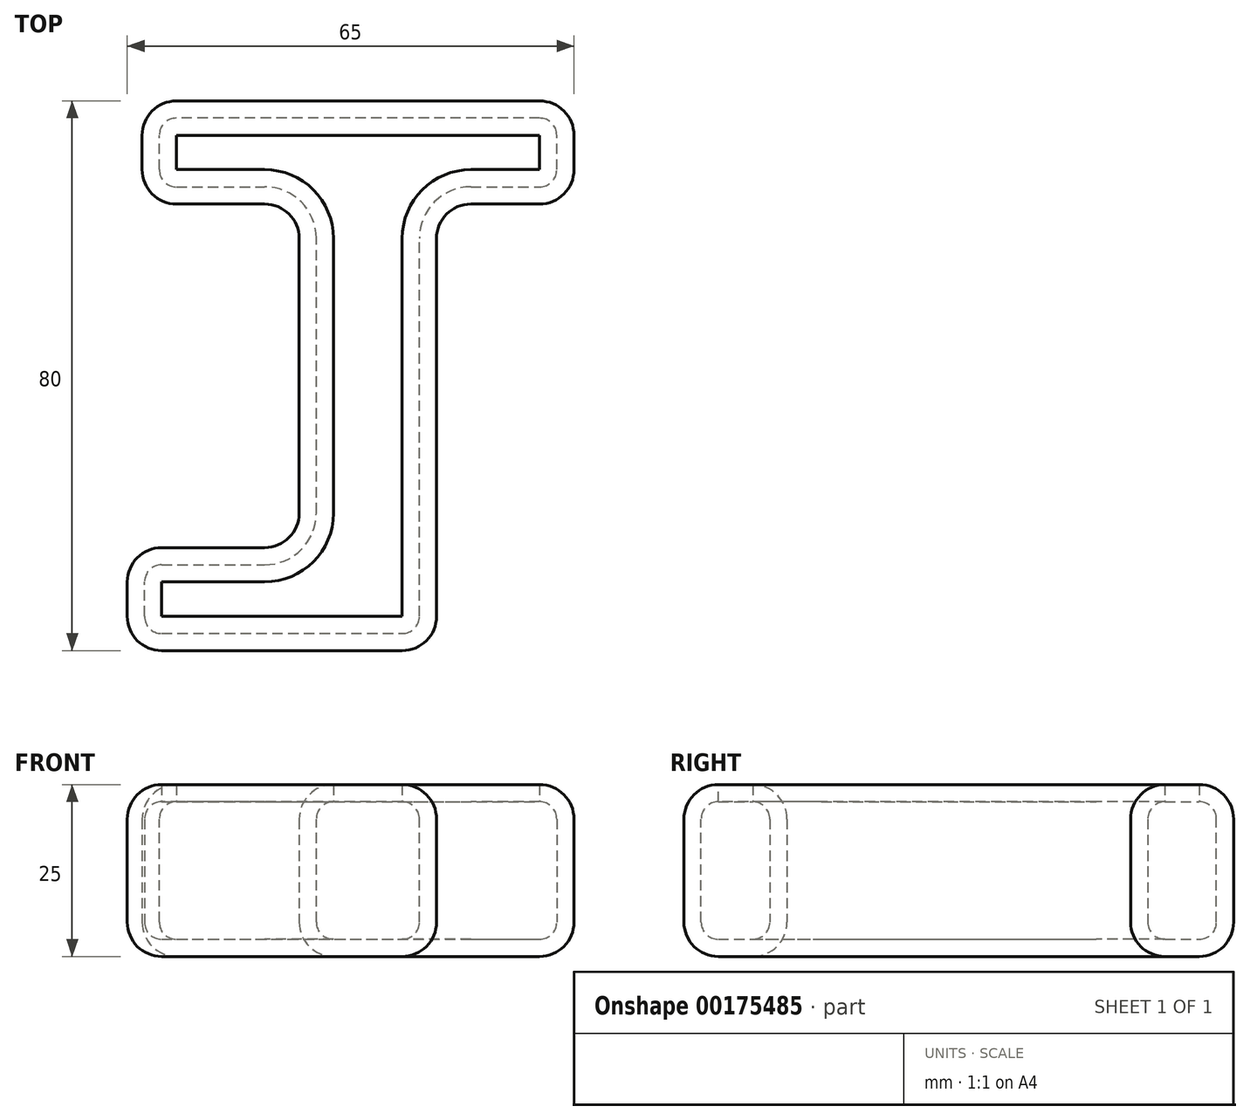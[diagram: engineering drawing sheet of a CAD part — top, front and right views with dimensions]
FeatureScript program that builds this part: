
annotation { "Feature Type Name" : "Feature", "Feature Type Description" : "" }
export const myFeature = defineFeature(function(context is Context, id is Id, definition is map)
    precondition{}
    {
        {
            var Q0;
            Q0=qCreatedBy(makeId("Top.planeOp"),FACE);
            var sketch = newSketch(context, id + "F0", { "sketchPlane" : qUnion([Q0])});
            skLineSegment(sketch, "E0.top", {"start": v(-12.6, -44.55) * mm, "end": v(7.4, -44.55) * mm});
            skLineSegment(sketch, "E0.left", {"start": v(-12.6, 20.45) * mm, "end": v(-12.6, -29.55) * mm});
            skLineSegment(sketch, "E0.right", {"start": v(7.4, 20.45) * mm, "end": v(7.4, -44.55) * mm});
            skLineSegment(sketch, "E1", {"start": v(-12.6, -29.55) * mm, "end": v(-37.6, -29.55) * mm});
            skLineSegment(sketch, "E2", {"start": v(-37.6, -29.55) * mm, "end": v(-37.6, -44.55) * mm});
            skLineSegment(sketch, "E3", {"start": v(-37.6, -44.55) * mm, "end": v(-12.6, -44.55) * mm});
            skLineSegment(sketch, "E4", {"start": v(-12.6, 20.45) * mm, "end": v(-35.44, 20.45) * mm});
            skLineSegment(sketch, "E5", {"start": v(-35.44, 20.45) * mm, "end": v(-35.44, 35.45) * mm});
            skLineSegment(sketch, "E6", {"start": v(-35.44, 35.45) * mm, "end": v(27.4, 35.45) * mm});
            skLineSegment(sketch, "E7", {"start": v(27.4, 35.45) * mm, "end": v(27.4, 20.45) * mm});
            skLineSegment(sketch, "E8", {"start": v(27.4, 20.45) * mm, "end": v(7.4, 20.45) * mm});
            skSolve(sketch);
        }
        {
            var Q0;
            Q0=makeQuery(id+"F0.imprint","IMPRINT",FACE,{"disambiguationData":[TD([[makeQuery(id+"F0.imprint","IMPRINT",EDGE,{"derivedFrom":sQuery(id+"F0.wireOp",EDGE,"E0.top")}),1.0]])]});
            extrude(context, id + "F1", {"entities" : qUnion([Q0]), "depth" : 25 * mm});
        }
        {
            var Q0;
            Q0=makeQuery(id+"F1.opExtrude","SWEPT_FACE",FACE,{"disambiguationData":[OSD([sQuery(id+"F0.wireOp",EDGE,"E4")])]});
            var Q1;
            Q1=makeQuery(id+"F1.opExtrude","SWEPT_FACE",FACE,{"disambiguationData":[OSD([sQuery(id+"F0.wireOp",EDGE,"E0.right")])]});
            var Q2;
            Q2=makeQuery(id+"F1.opExtrude","SWEPT_FACE",FACE,{"disambiguationData":[OSD([sQuery(id+"F0.wireOp",EDGE,"E0.top"),sQuery(id+"F0.wireOp",EDGE,"E3")])]});
            var Q3;
            Q3=makeQuery(id+"F1.opExtrude","SWEPT_FACE",FACE,{"disambiguationData":[OSD([sQuery(id+"F0.wireOp",EDGE,"E2")])]});
            var Q4;
            Q4=makeQuery(id+"F1.opExtrude","SWEPT_FACE",FACE,{"disambiguationData":[OSD([sQuery(id+"F0.wireOp",EDGE,"E1")])]});
            var Q5;
            Q5=makeQuery(id+"F1.opExtrude","CAP_FACE",FACE,{"disambiguationData":[OSD([sQuery(id+"F0.wireOp",EDGE,"E0.top"),sQuery(id+"F0.wireOp",EDGE,"E0.left"),sQuery(id+"F0.wireOp",EDGE,"E0.right"),sQuery(id+"F0.wireOp",EDGE,"E1"),sQuery(id+"F0.wireOp",EDGE,"E2"),sQuery(id+"F0.wireOp",EDGE,"E3"),sQuery(id+"F0.wireOp",EDGE,"E4"),sQuery(id+"F0.wireOp",EDGE,"E5"),sQuery(id+"F0.wireOp",EDGE,"E6"),sQuery(id+"F0.wireOp",EDGE,"E7"),sQuery(id+"F0.wireOp",EDGE,"E8")])],"isStart":false});
            var Q6;
            Q6=makeQuery(id+"F1.opExtrude","SWEPT_FACE",FACE,{"disambiguationData":[OSD([sQuery(id+"F0.wireOp",EDGE,"E6")])]});
            var Q7;
            Q7=makeQuery(id+"F1.opExtrude","SWEPT_FACE",FACE,{"disambiguationData":[OSD([sQuery(id+"F0.wireOp",EDGE,"E7")])]});
            var Q8;
            Q8=makeQuery(id+"F1.opExtrude","CAP_FACE",FACE,{"disambiguationData":[OSD([sQuery(id+"F0.wireOp",EDGE,"E0.top"),sQuery(id+"F0.wireOp",EDGE,"E0.left"),sQuery(id+"F0.wireOp",EDGE,"E0.right"),sQuery(id+"F0.wireOp",EDGE,"E1"),sQuery(id+"F0.wireOp",EDGE,"E2"),sQuery(id+"F0.wireOp",EDGE,"E3"),sQuery(id+"F0.wireOp",EDGE,"E4"),sQuery(id+"F0.wireOp",EDGE,"E5"),sQuery(id+"F0.wireOp",EDGE,"E6"),sQuery(id+"F0.wireOp",EDGE,"E7"),sQuery(id+"F0.wireOp",EDGE,"E8")])],"isStart":true});
            fillet(context, id + "F2", {"entities" : qUnion([Q0, Q1, Q2, Q3, Q4, Q5, Q6, Q7, Q8]), "radius" : 5 * mm, "tangentPropagation" : true, "allowEdgeOverflow" : false});
        }
        {
            var Q0;
            Q0=makeQuery(id+"F1.opExtrude","CAP_FACE",FACE,{"disambiguationData":[OSD([sQuery(id+"F0.wireOp",EDGE,"E0.top"),sQuery(id+"F0.wireOp",EDGE,"E0.left"),sQuery(id+"F0.wireOp",EDGE,"E0.right"),sQuery(id+"F0.wireOp",EDGE,"E1"),sQuery(id+"F0.wireOp",EDGE,"E2"),sQuery(id+"F0.wireOp",EDGE,"E3"),sQuery(id+"F0.wireOp",EDGE,"E4"),sQuery(id+"F0.wireOp",EDGE,"E5"),sQuery(id+"F0.wireOp",EDGE,"E6"),sQuery(id+"F0.wireOp",EDGE,"E7"),sQuery(id+"F0.wireOp",EDGE,"E8")])],"isStart":false});
            shell(context, id + "F3", {"entities" : qUnion([Q0]), "thickness" : 2.5 * mm});
        }
    });
